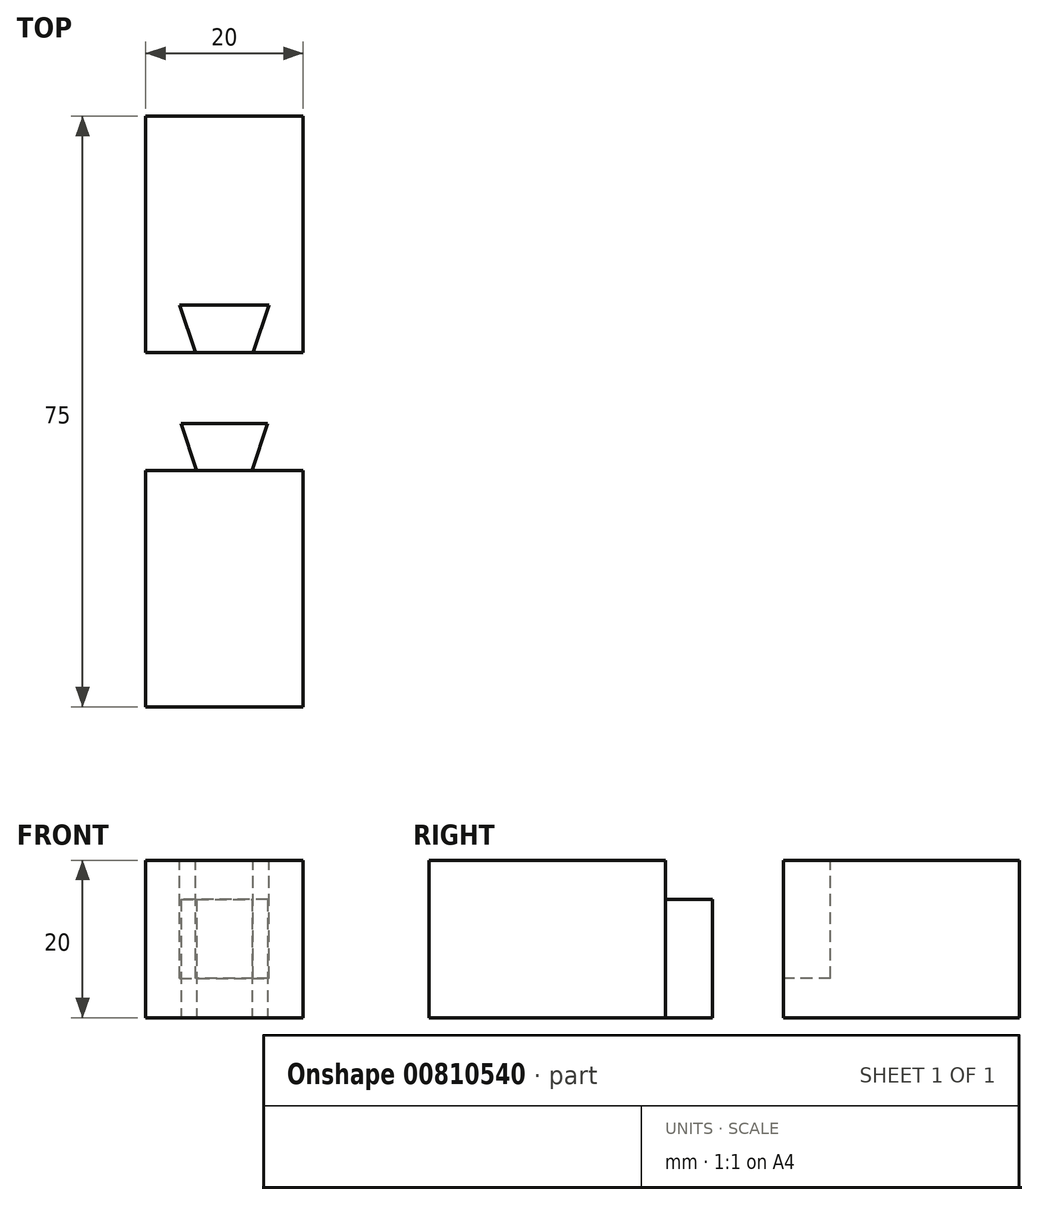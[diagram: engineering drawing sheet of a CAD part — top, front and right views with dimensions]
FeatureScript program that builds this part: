
annotation { "Feature Type Name" : "Feature", "Feature Type Description" : "" }
export const myFeature = defineFeature(function(context is Context, id is Id, definition is map)
    precondition{}
    {
        {
            var Q0;
            Q0=qCreatedBy(makeId("Front.planeOp"),FACE);
            var sketch = newSketch(context, id + "F0", { "sketchPlane" : qUnion([Q0])});
            skLineSegment(sketch, "E0.bottom", {"start": v(10, 10) * mm, "end": v(-10, 10) * mm});
            skLineSegment(sketch, "E0.top", {"start": v(10, -10) * mm, "end": v(-10, -10) * mm});
            skLineSegment(sketch, "E0.left", {"start": v(10, 10) * mm, "end": v(10, -10) * mm});
            skLineSegment(sketch, "E0.right", {"start": v(-10, 10) * mm, "end": v(-10, -10) * mm});
            skPoint(sketch, "E0.middle", {"position": v(0, 0) * mm});
            skSolve(sketch);
        }
        {
            var Q0;
            Q0=makeQuery(id+"F0.imprint","IMPRINT",FACE,{"disambiguationData":[TD([[makeQuery(id+"F0.imprint","IMPRINT",EDGE,{"derivedFrom":sQuery(id+"F0.wireOp",EDGE,"E0.bottom")}),1.0]])]});
            extrude(context, id + "F1", {"entities" : qUnion([Q0]), "depth" : 30 * mm, "offsetDistance" : 25 * mm});
        }
        {
            var Q0;
            Q0=makeQuery(id+"F1.opExtrude","SWEPT_FACE",FACE,{"disambiguationData":[OSD([sQuery(id+"F0.wireOp",EDGE,"E0.bottom")])]});
            var sketch = newSketch(context, id + "F2", { "sketchPlane" : qUnion([Q0])});
            skLineSegment(sketch, "E1.bottom", {"start": v(3.5, 0) * mm, "end": v(-3.5, 0) * mm});
            skLineSegment(sketch, "E2", {"start": v(-5.5, 6) * mm, "end": v(5.5, 6) * mm});
            skLineSegment(sketch, "E3", {"start": v(5.5, 6) * mm, "end": v(3.5, 0) * mm});
            skLineSegment(sketch, "E4", {"start": v(-5.5, 6) * mm, "end": v(-3.5, 0) * mm});
            skPoint(sketch, "E5", {"position": v(0, 0) * mm});
            skSolve(sketch);
        }
        {
            var Q0;
            Q0=qSketchRegion(id+"F2",true);
            var Q1;
            Q1=makeQuery(id+"F1.opExtrude","SWEPT_FACE",FACE,{"disambiguationData":[OSD([sQuery(id+"F0.wireOp",EDGE,"E0.top")])]});
            extrude(context, id + "F3", {"entities" : qUnion([Q0]), "operationType" : NewBodyOperationType.ADD, "oppositeDirection" : true, "depth" : 15 * mm, "endBoundEntityFace" : qUnion([Q1]), "offsetDistance" : 25 * mm});
        }
        {
            var Q0;
            Q0=makeQuery(id+"F3.boolean.opBoolean","MERGE",FACE,{"derivedFrom":[makeQuery(id+"F1.opExtrude","SWEPT_FACE",FACE,{"disambiguationData":[OSD([sQuery(id+"F0.wireOp",EDGE,"E0.bottom")])]}),makeQuery(id+"F3.opExtrude","CAP_FACE",FACE,{"disambiguationData":[OSD([sQuery(id+"F2.wireOp",EDGE,"E1.bottom"),sQuery(id+"F2.wireOp",EDGE,"E2"),sQuery(id+"F2.wireOp",EDGE,"E3"),sQuery(id+"F2.wireOp",EDGE,"E4")])],"isStart":true})]});
            var sketch = newSketch(context, id + "F4", { "sketchPlane" : qUnion([Q0])});
            skLineSegment(sketch, "E6", {"start": v(-6.5, 9) * mm, "end": v(6.5, 9) * mm});
            skLineSegment(sketch, "E7", {"start": v(6.5, 9) * mm, "end": v(6.5, 0) * mm});
            skLineSegment(sketch, "E8", {"start": v(-6.5, 9) * mm, "end": v(-6.5, 0) * mm});
            skLineSegment(sketch, "E9", {"start": v(-6.5, 0) * mm, "end": v(6.5, 0) * mm});
            skPoint(sketch, "E10", {"position": v(0, 0) * mm});
            skSolve(sketch);
        }
        {
            var Q0;
            Q0=qCreatedBy(makeId("Front.planeOp"),FACE);
            var sketch = newSketch(context, id + "F5", { "sketchPlane" : qUnion([Q0])});
            skPoint(sketch, "E11.middle", {"position": v(0, 0) * mm});
            skLineSegment(sketch, "E12.bottom", {"start": v(10, 10) * mm, "end": v(-10, 10) * mm});
            skLineSegment(sketch, "E12.top", {"start": v(10, -10) * mm, "end": v(-10, -10) * mm});
            skLineSegment(sketch, "E12.left", {"start": v(10, 10) * mm, "end": v(10, -10) * mm});
            skLineSegment(sketch, "E12.right", {"start": v(-10, 10) * mm, "end": v(-10, -10) * mm});
            skSolve(sketch);
        }
        {
            var Q0;
            Q0=qSketchRegion(id+"F5",true);
            extrude(context, id + "F6", {"entities" : qUnion([Q0]), "oppositeDirection" : true, "depth" : 30 * mm, "offsetDistance" : 25 * mm});
        }
        {
            var Q0;
            Q0=makeQuery(id+"F1.opExtrude","SWEPT_BODY",BODY,{"disambiguationData":[OSD([sQuery(id+"F0.wireOp",EDGE,"E0.bottom"),sQuery(id+"F0.wireOp",EDGE,"E0.top"),sQuery(id+"F0.wireOp",EDGE,"E0.left"),sQuery(id+"F0.wireOp",EDGE,"E0.right")])]});
            var Q1;
            Q1=makeQuery(id+"F6.opExtrude","SWEPT_BODY",BODY,{"disambiguationData":[OSD([sQuery(id+"F5.wireOp",EDGE,"E12.bottom"),sQuery(id+"F5.wireOp",EDGE,"E12.top"),sQuery(id+"F5.wireOp",EDGE,"E12.left"),sQuery(id+"F5.wireOp",EDGE,"E12.right")])]});
            var Q2;
            Q2=makeQuery(id+"F3.opExtrude","SWEPT_FACE",FACE,{"disambiguationData":[OSD([sQuery(id+"F2.wireOp",EDGE,"E4")])]});
            var Q3;
            Q3=makeQuery(id+"F3.opExtrude","SWEPT_FACE",FACE,{"disambiguationData":[OSD([sQuery(id+"F2.wireOp",EDGE,"E3")])]});
            booleanBodies(context, id + "F7", {"operationType" : BooleanOperationType.SUBTRACTION, "tools" : qUnion([Q0]), "targets" : qUnion([Q1]), "offset" : true, "entitiesToOffset" : qUnion([Q2, Q3]), "offsetDistance" : 0.15 * mm, "keepTools" : true});
        }
        {
            var Q0;
            Q0=makeQuery(id+"F6.opExtrude","SWEPT_BODY",BODY,{"disambiguationData":[OSD([sQuery(id+"F5.wireOp",EDGE,"E12.bottom"),sQuery(id+"F5.wireOp",EDGE,"E12.top"),sQuery(id+"F5.wireOp",EDGE,"E12.left"),sQuery(id+"F5.wireOp",EDGE,"E12.right")])]});
            transform(context, id + "F8", {"entities" : qUnion([Q0]), "transformType" : TransformType.TRANSLATION_3D, "dx" : 0 * mm, "dy" : 15 * mm, "dz" : 0 * mm, "makeCopy" : false});
        }
        {
            var Q0;
            Q0=makeQuery(id+"F1.opExtrude","SWEPT_BODY",BODY,{"disambiguationData":[OSD([sQuery(id+"F0.wireOp",EDGE,"E0.bottom"),sQuery(id+"F0.wireOp",EDGE,"E0.top"),sQuery(id+"F0.wireOp",EDGE,"E0.left"),sQuery(id+"F0.wireOp",EDGE,"E0.right")])]});
            var Q1;
            Q1=makeQuery(id+"F1.opExtrude","SWEPT_EDGE",EDGE,{"disambiguationData":[OSD([sQuery(id+"F0.wireOp",EDGE,"E0.bottom"),sQuery(id+"F0.wireOp",EDGE,"E0.right")])]});
            transform(context, id + "F9", {"entities" : qUnion([Q0]), "transformType" : TransformType.ROTATION, "transformAxis" : qUnion([Q1]), "angle" : 180 * degree, "makeCopy" : false});
        }
        {
            var Q0;
            Q0=makeQuery(id+"F1.opExtrude","SWEPT_BODY",BODY,{"disambiguationData":[OSD([sQuery(id+"F0.wireOp",EDGE,"E0.bottom"),sQuery(id+"F0.wireOp",EDGE,"E0.top"),sQuery(id+"F0.wireOp",EDGE,"E0.left"),sQuery(id+"F0.wireOp",EDGE,"E0.right")])]});
            transform(context, id + "F10", {"entities" : qUnion([Q0]), "transformType" : TransformType.TRANSLATION_3D, "dx" : 20 * mm, "dy" : 0 * mm, "dz" : -20 * mm, "makeCopy" : false});
        }
    });
